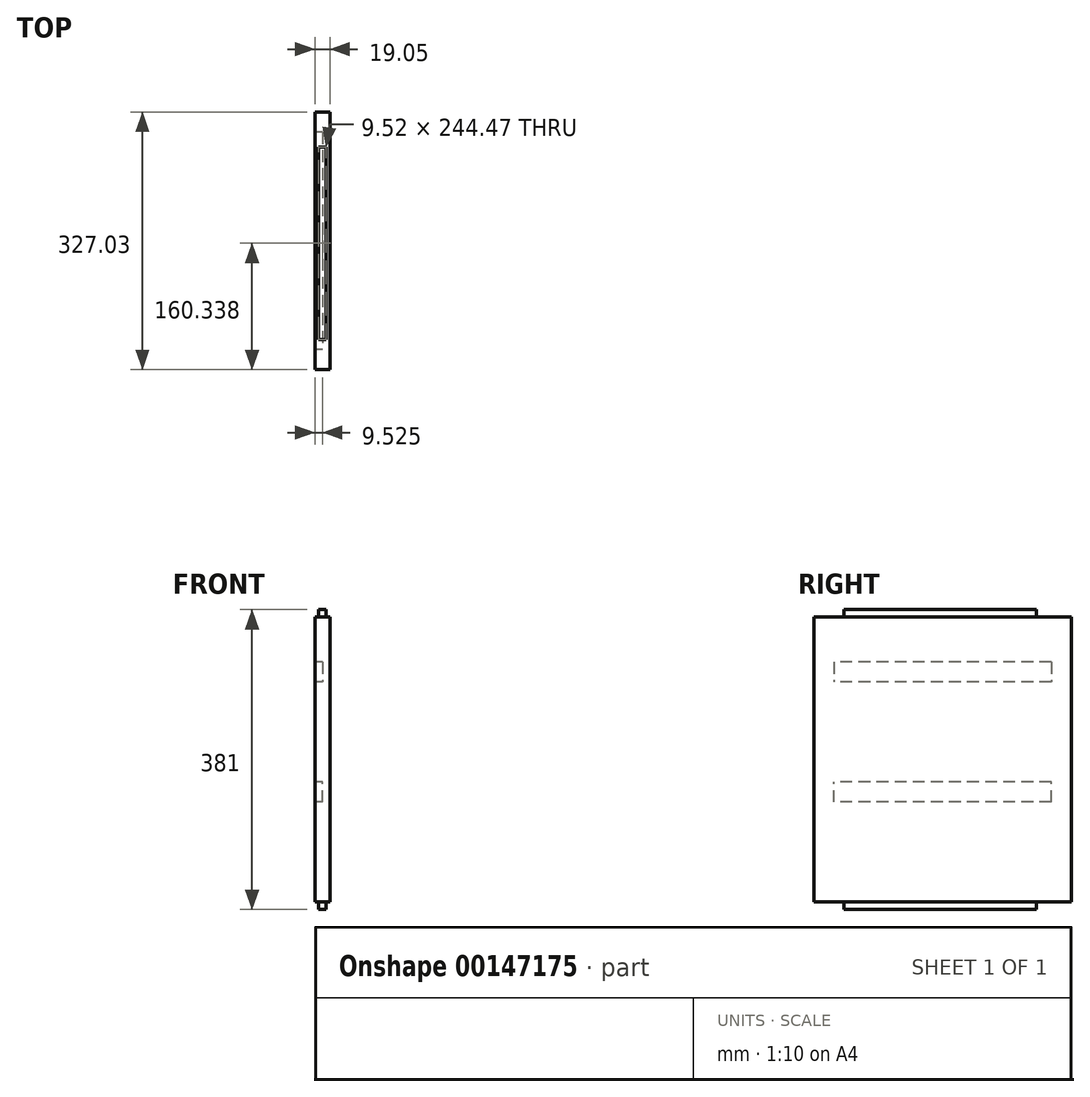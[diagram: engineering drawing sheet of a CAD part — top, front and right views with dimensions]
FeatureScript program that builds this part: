
annotation { "Feature Type Name" : "Feature", "Feature Type Description" : "" }
export const myFeature = defineFeature(function(context is Context, id is Id, definition is map)
    precondition{}
    {
        {
            var Q0;
            Q0=qCreatedBy(makeId("Right.planeOp"),FACE);
            var sketch = newSketch(context, id + "F0", { "sketchPlane" : qUnion([Q0])});
            skLineSegment(sketch, "E0.bottom", {"start": v(0, 0) * mm, "end": v(327.03, 0) * mm});
            skLineSegment(sketch, "E0.top", {"start": v(0, 381) * mm, "end": v(327.02, 381) * mm});
            skLineSegment(sketch, "E0.left", {"start": v(0, 0) * mm, "end": v(0, 381) * mm});
            skLineSegment(sketch, "E0.right", {"start": v(327.03, 0) * mm, "end": v(327.02, 381) * mm});
            skSolve(sketch);
        }
        {
            var Q0;
            Q0=makeQuery(id+"F0.imprint","IMPRINT",FACE,{"disambiguationData":[TD([[makeQuery(id+"F0.imprint","IMPRINT",EDGE,{"derivedFrom":sQuery(id+"F0.wireOp",EDGE,"E0.bottom")}),1.0]])]});
            extrude(context, id + "F1", {"entities" : qUnion([Q0]), "depth" : 19.05 * mm});
        }
        {
            var Q0;
            Q0=qCreatedBy(makeId("Front.planeOp"),FACE);
            var sketch = newSketch(context, id + "F2", { "sketchPlane" : qUnion([Q0])});
            skLineSegment(sketch, "E1.bottom", {"start": v(0, 0) * mm, "end": v(4.76, 0) * mm});
            skLineSegment(sketch, "E1.top", {"start": v(0, 9.52) * mm, "end": v(4.76, 9.52) * mm});
            skLineSegment(sketch, "E1.left", {"start": v(0, 0) * mm, "end": v(0, 9.52) * mm});
            skLineSegment(sketch, "E1.right", {"start": v(4.76, 0) * mm, "end": v(4.76, 9.52) * mm});
            skLineSegment(sketch, "E2.bottom", {"start": v(19.05, 0) * mm, "end": v(14.29, 0) * mm});
            skLineSegment(sketch, "E2.top", {"start": v(19.05, 9.52) * mm, "end": v(14.29, 9.52) * mm});
            skLineSegment(sketch, "E2.left", {"start": v(19.05, 0) * mm, "end": v(19.05, 9.52) * mm});
            skLineSegment(sketch, "E2.right", {"start": v(14.29, 0) * mm, "end": v(14.29, 9.52) * mm});
            skLineSegment(sketch, "E3.bottom", {"start": v(0, 381) * mm, "end": v(4.76, 381) * mm});
            skLineSegment(sketch, "E3.top", {"start": v(0, 371.48) * mm, "end": v(4.76, 371.48) * mm});
            skLineSegment(sketch, "E3.left", {"start": v(0, 381) * mm, "end": v(0, 371.48) * mm});
            skLineSegment(sketch, "E3.right", {"start": v(4.76, 381) * mm, "end": v(4.76, 371.48) * mm});
            skLineSegment(sketch, "E4.bottom", {"start": v(14.29, 371.48) * mm, "end": v(19.05, 371.48) * mm});
            skLineSegment(sketch, "E4.top", {"start": v(14.29, 381) * mm, "end": v(19.05, 381) * mm});
            skLineSegment(sketch, "E4.left", {"start": v(14.29, 371.48) * mm, "end": v(14.29, 381) * mm});
            skLineSegment(sketch, "E4.right", {"start": v(19.05, 371.48) * mm, "end": v(19.05, 381) * mm});
            skSolve(sketch);
        }
        {
            var Q0;
            Q0=makeQuery(id+"F2.imprint","IMPRINT",FACE,{"disambiguationData":[TD([[makeQuery(id+"F2.imprint","IMPRINT",EDGE,{"derivedFrom":sQuery(id+"F2.wireOp",EDGE,"E3.bottom")}),-1.0]])]});
            var Q1;
            Q1=makeQuery(id+"F2.imprint","IMPRINT",FACE,{"disambiguationData":[TD([[makeQuery(id+"F2.imprint","IMPRINT",EDGE,{"derivedFrom":sQuery(id+"F2.wireOp",EDGE,"E4.bottom")}),1.0]])]});
            var Q2;
            Q2=makeQuery(id+"F2.imprint","IMPRINT",FACE,{"disambiguationData":[TD([[makeQuery(id+"F2.imprint","IMPRINT",EDGE,{"derivedFrom":sQuery(id+"F2.wireOp",EDGE,"E1.bottom")}),1.0]])]});
            var Q3;
            Q3=makeQuery(id+"F2.imprint","IMPRINT",FACE,{"disambiguationData":[TD([[makeQuery(id+"F2.imprint","IMPRINT",EDGE,{"derivedFrom":sQuery(id+"F2.wireOp",EDGE,"E2.bottom")}),-1.0]])]});
            extrude(context, id + "F3", {"entities" : qUnion([Q0, Q1, Q2, Q3]), "operationType" : NewBodyOperationType.REMOVE, "endBound" : BoundingType.UP_TO_NEXT, "oppositeDirection" : true, "depth" : 25.4 * mm});
        }
        {
            var Q0;
            Q0=makeQuery(id+"F3.boolean.opBoolean","COPY",FACE,{"derivedFrom":makeQuery(id+"F3.opExtrude","SWEPT_FACE",FACE,{"disambiguationData":[OSD([sQuery(id+"F2.wireOp",EDGE,"E4.left")])]})});
            var sketch = newSketch(context, id + "F4", { "sketchPlane" : qUnion([Q0])});
            skLineSegment(sketch, "E5.bottom", {"start": v(0, 381) * mm, "end": v(38.1, 381) * mm});
            skLineSegment(sketch, "E5.top", {"start": v(0, 371.48) * mm, "end": v(38.1, 371.48) * mm});
            skLineSegment(sketch, "E5.left", {"start": v(0, 381) * mm, "end": v(0, 371.48) * mm});
            skLineSegment(sketch, "E5.right", {"start": v(38.1, 381) * mm, "end": v(38.1, 371.48) * mm});
            skLineSegment(sketch, "E6.bottom", {"start": v(38.1, 9.53) * mm, "end": v(0, 9.53) * mm});
            skLineSegment(sketch, "E6.top", {"start": v(38.1, 0) * mm, "end": v(0, 0) * mm});
            skLineSegment(sketch, "E6.left", {"start": v(38.1, 9.53) * mm, "end": v(38.1, 0) * mm});
            skLineSegment(sketch, "E6.right", {"start": v(0, 9.53) * mm, "end": v(0, 0) * mm});
            skLineSegment(sketch, "E7.bottom", {"start": v(327.02, 0) * mm, "end": v(282.57, 0) * mm});
            skLineSegment(sketch, "E7.top", {"start": v(327.02, 9.53) * mm, "end": v(282.57, 9.52) * mm});
            skLineSegment(sketch, "E7.left", {"start": v(327.02, 0) * mm, "end": v(327.02, 9.53) * mm});
            skLineSegment(sketch, "E7.right", {"start": v(282.57, 0) * mm, "end": v(282.57, 9.52) * mm});
            skLineSegment(sketch, "E8.bottom", {"start": v(327.02, 371.48) * mm, "end": v(282.57, 371.48) * mm});
            skLineSegment(sketch, "E8.top", {"start": v(327.02, 381) * mm, "end": v(282.57, 381) * mm});
            skLineSegment(sketch, "E8.left", {"start": v(327.02, 371.48) * mm, "end": v(327.02, 381) * mm});
            skLineSegment(sketch, "E8.right", {"start": v(282.57, 371.48) * mm, "end": v(282.57, 381) * mm});
            skSolve(sketch);
        }
        {
            var Q0;
            Q0=makeQuery(id+"F4.imprint","IMPRINT",FACE,{"disambiguationData":[TD([[makeQuery(id+"F4.imprint","IMPRINT",EDGE,{"derivedFrom":sQuery(id+"F4.wireOp",EDGE,"E5.bottom")}),1.0]])]});
            var Q1;
            Q1=makeQuery(id+"F4.imprint","IMPRINT",FACE,{"disambiguationData":[TD([[makeQuery(id+"F4.imprint","IMPRINT",EDGE,{"derivedFrom":sQuery(id+"F4.wireOp",EDGE,"E6.bottom")}),1.0]])]});
            var Q2;
            Q2=makeQuery(id+"F4.imprint","IMPRINT",FACE,{"disambiguationData":[TD([[makeQuery(id+"F4.imprint","IMPRINT",EDGE,{"derivedFrom":sQuery(id+"F4.wireOp",EDGE,"E8.bottom")}),-1.0]])]});
            var Q3;
            Q3=makeQuery(id+"F4.imprint","IMPRINT",FACE,{"disambiguationData":[TD([[makeQuery(id+"F4.imprint","IMPRINT",EDGE,{"derivedFrom":sQuery(id+"F4.wireOp",EDGE,"E7.bottom")}),-1.0]])]});
            extrude(context, id + "F5", {"entities" : qUnion([Q0, Q1, Q2, Q3]), "operationType" : NewBodyOperationType.REMOVE, "endBound" : BoundingType.UP_TO_NEXT, "oppositeDirection" : true, "depth" : 25.4 * mm});
        }
        {
            var Q0;
            Q0=makeQuery(id+"F1.opExtrude","CAP_FACE",FACE,{"disambiguationData":[OSD([sQuery(id+"F0.wireOp",EDGE,"E0.bottom"),sQuery(id+"F0.wireOp",EDGE,"E0.top"),sQuery(id+"F0.wireOp",EDGE,"E0.left"),sQuery(id+"F0.wireOp",EDGE,"E0.right")])],"isStart":true});
            var sketch = newSketch(context, id + "F6", { "sketchPlane" : qUnion([Q0])});
            skLineSegment(sketch, "E9.bottom", {"start": v(-301.62, 314.33) * mm, "end": v(-25.4, 314.33) * mm});
            skLineSegment(sketch, "E9.top", {"start": v(-301.62, 288.93) * mm, "end": v(-25.4, 288.93) * mm});
            skLineSegment(sketch, "E9.left", {"start": v(-301.62, 314.33) * mm, "end": v(-301.62, 288.93) * mm});
            skLineSegment(sketch, "E9.right", {"start": v(-25.4, 314.33) * mm, "end": v(-25.4, 288.93) * mm});
            skLineSegment(sketch, "E10.bottom", {"start": v(-301.62, 136.53) * mm, "end": v(-25.4, 136.53) * mm});
            skLineSegment(sketch, "E10.top", {"start": v(-301.62, 161.93) * mm, "end": v(-25.4, 161.93) * mm});
            skLineSegment(sketch, "E10.left", {"start": v(-301.62, 136.53) * mm, "end": v(-301.62, 161.93) * mm});
            skLineSegment(sketch, "E10.right", {"start": v(-25.4, 136.53) * mm, "end": v(-25.4, 161.93) * mm});
            skSolve(sketch);
        }
        {
            var Q0;
            Q0=makeQuery(id+"F6.imprint","IMPRINT",FACE,{"disambiguationData":[TD([[makeQuery(id+"F6.imprint","IMPRINT",EDGE,{"derivedFrom":sQuery(id+"F6.wireOp",EDGE,"E9.bottom")}),-1.0]])]});
            var Q1;
            Q1=makeQuery(id+"F6.imprint","IMPRINT",FACE,{"disambiguationData":[TD([[makeQuery(id+"F6.imprint","IMPRINT",EDGE,{"derivedFrom":sQuery(id+"F6.wireOp",EDGE,"E10.bottom")}),1.0]])]});
            extrude(context, id + "F7", {"entities" : qUnion([Q0, Q1]), "operationType" : NewBodyOperationType.REMOVE, "oppositeDirection" : true, "depth" : 9.52 * mm});
        }
    });
